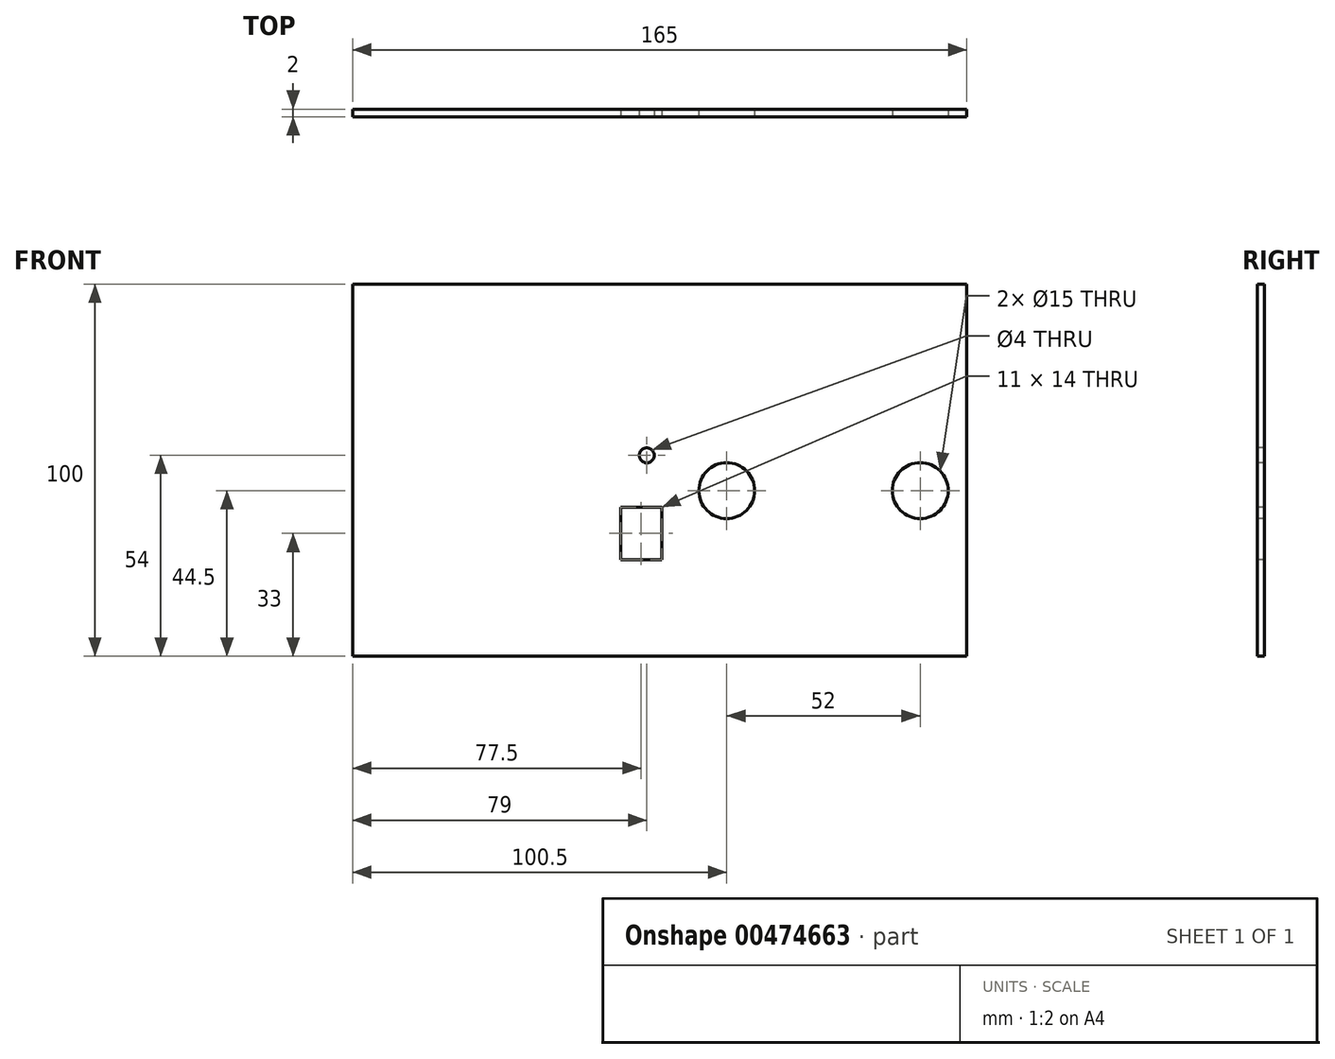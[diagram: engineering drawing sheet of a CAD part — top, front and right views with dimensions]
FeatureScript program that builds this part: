
annotation { "Feature Type Name" : "Feature", "Feature Type Description" : "" }
export const myFeature = defineFeature(function(context is Context, id is Id, definition is map)
    precondition{}
    {
        {
            var Q0;
            Q0=qCreatedBy(makeId("Front.planeOp"),FACE);
            var sketch = newSketch(context, id + "F0", { "sketchPlane" : qUnion([Q0])});
            skLineSegment(sketch, "E0.bottom", {"start": v(82.5, 50) * mm, "end": v(-82.5, 50) * mm});
            skLineSegment(sketch, "E0.top", {"start": v(82.5, -50) * mm, "end": v(-82.5, -50) * mm});
            skLineSegment(sketch, "E0.left", {"start": v(82.5, 50) * mm, "end": v(82.5, -50) * mm});
            skLineSegment(sketch, "E0.right", {"start": v(-82.5, 50) * mm, "end": v(-82.5, -50) * mm});
            skPoint(sketch, "E0.middle", {"position": v(0, 0) * mm});
            skSolve(sketch);
        }
        {
            var Q0;
            Q0=makeQuery(id+"F0.imprint","IMPRINT",FACE,{"disambiguationData":[TD([[makeQuery(id+"F0.imprint","IMPRINT",EDGE,{"derivedFrom":sQuery(id+"F0.wireOp",EDGE,"E0.bottom")}),1.0]])]});
            extrude(context, id + "F1", {"entities" : qUnion([Q0]), "depth" : 2 * mm});
        }
        {
            var Q0;
            Q0=makeQuery(id+"F1.opExtrude","CAP_FACE",FACE,{"disambiguationData":[OSD([sQuery(id+"F0.wireOp",EDGE,"E0.bottom"),sQuery(id+"F0.wireOp",EDGE,"E0.top"),sQuery(id+"F0.wireOp",EDGE,"E0.left"),sQuery(id+"F0.wireOp",EDGE,"E0.right")])],"isStart":false});
            var sketch = newSketch(context, id + "F2", { "sketchPlane" : qUnion([Q0])});
            skLineSegment(sketch, "E1.bottom", {"start": v(0.5, -24) * mm, "end": v(-10.5, -24) * mm});
            skLineSegment(sketch, "E1.top", {"start": v(0.5, -10) * mm, "end": v(-10.5, -10) * mm});
            skLineSegment(sketch, "E1.left", {"start": v(0.5, -24) * mm, "end": v(0.5, -10) * mm});
            skLineSegment(sketch, "E1.right", {"start": v(-10.5, -24) * mm, "end": v(-10.5, -10) * mm});
            skPoint(sketch, "E1.middle", {"position": v(-5, -17) * mm});
            skCircle(sketch, "E2", {"center": v(-3.5, 4) * mm, "radius": 2 * mm});
            skCircle(sketch, "E3", {"center": v(18, -5.5) * mm, "radius": 7.5 * mm});
            skCircle(sketch, "E4", {"center": v(70, -5.5) * mm, "radius": 7.5 * mm});
            skSolve(sketch);
        }
        {
            var Q0;
            Q0 = qSketchRegion(id + "F2", true);
            extrude(context, id + "F3", {"entities" : qUnion([Q0]), "operationType" : NewBodyOperationType.REMOVE, "oppositeDirection" : true, "depth" : 25 * mm});
        }
    });
